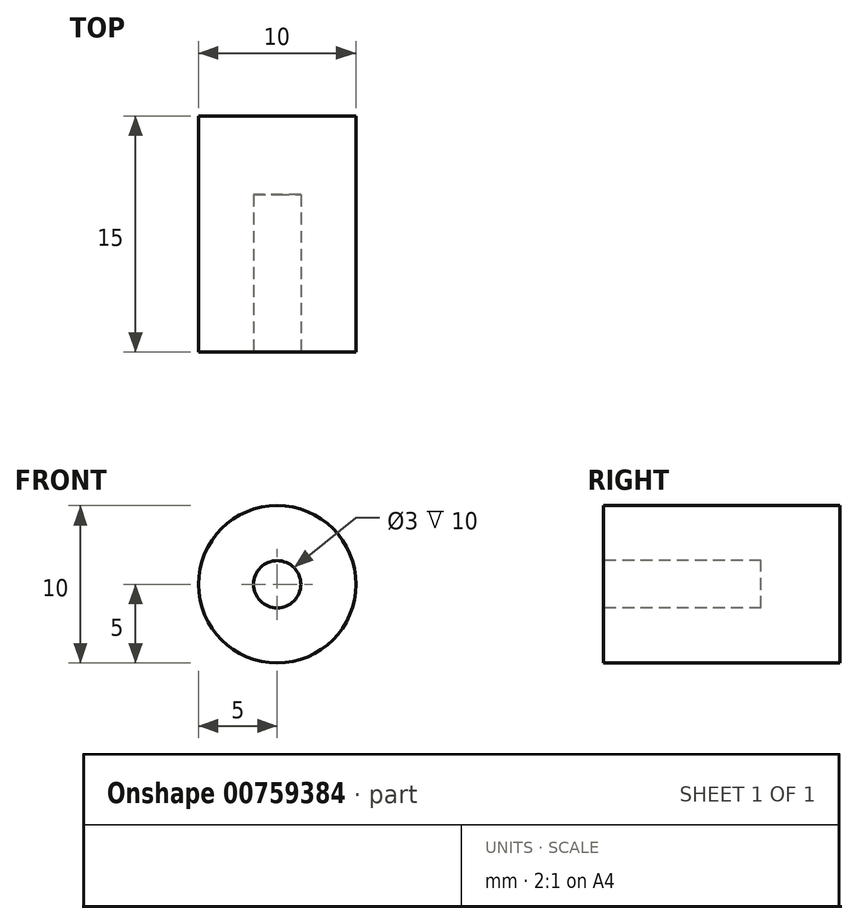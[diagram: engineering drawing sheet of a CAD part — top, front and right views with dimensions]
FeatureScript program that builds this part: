
annotation { "Feature Type Name" : "Feature", "Feature Type Description" : "" }
export const myFeature = defineFeature(function(context is Context, id is Id, definition is map)
    precondition{}
    {
        {
            var Q0;
            Q0=qCreatedBy(makeId("Front.planeOp"),FACE);
            var sketch = newSketch(context, id + "F0", { "sketchPlane" : qUnion([Q0])});
            skCircle(sketch, "E0", {"center": v(0, 0) * mm, "radius": 5 * mm});
            skCircle(sketch, "E1", {"center": v(0, 0) * mm, "radius": 1.5 * mm});
            skSolve(sketch);
        }
        {
            var Q0;
            Q0=makeQuery(id+"F0.imprint","IMPRINT",FACE,{"disambiguationData":[TD([[makeQuery(id+"F0.imprint","IMPRINT",EDGE,{"derivedFrom":sQuery(id+"F0.wireOp",EDGE,"E1")}),1.0]])]});
            var Q1;
            Q1=makeQuery(id+"F0.imprint","IMPRINT",FACE,{"disambiguationData":[TD([[makeQuery(id+"F0.imprint","IMPRINT",EDGE,{"derivedFrom":sQuery(id+"F0.wireOp",EDGE,"E0")}),1.0]])]});
            extrude(context, id + "F1", {"entities" : qUnion([Q0, Q1]), "oppositeDirection" : true, "depth" : 15 * mm, "offsetDistance" : 25 * mm});
        }
        {
            var Q0;
            Q0=makeQuery(id+"F1.opExtrude","CAP_FACE",FACE,{"disambiguationData":[OSD([sQuery(id+"F0.wireOp",EDGE,"E0")])],"isStart":true});
            var sketch = newSketch(context, id + "F2", { "sketchPlane" : qUnion([Q0])});
            skCircle(sketch, "E2", {"center": v(0, 0) * mm, "radius": 1.5 * mm});
            skSolve(sketch);
        }
        {
            var Q0;
            Q0 = qSketchRegion(id + "F2", true);
            extrude(context, id + "F3", {"entities" : qUnion([Q0]), "operationType" : NewBodyOperationType.REMOVE, "oppositeDirection" : true, "depth" : 10 * mm, "offsetDistance" : 25 * mm});
        }
    });
